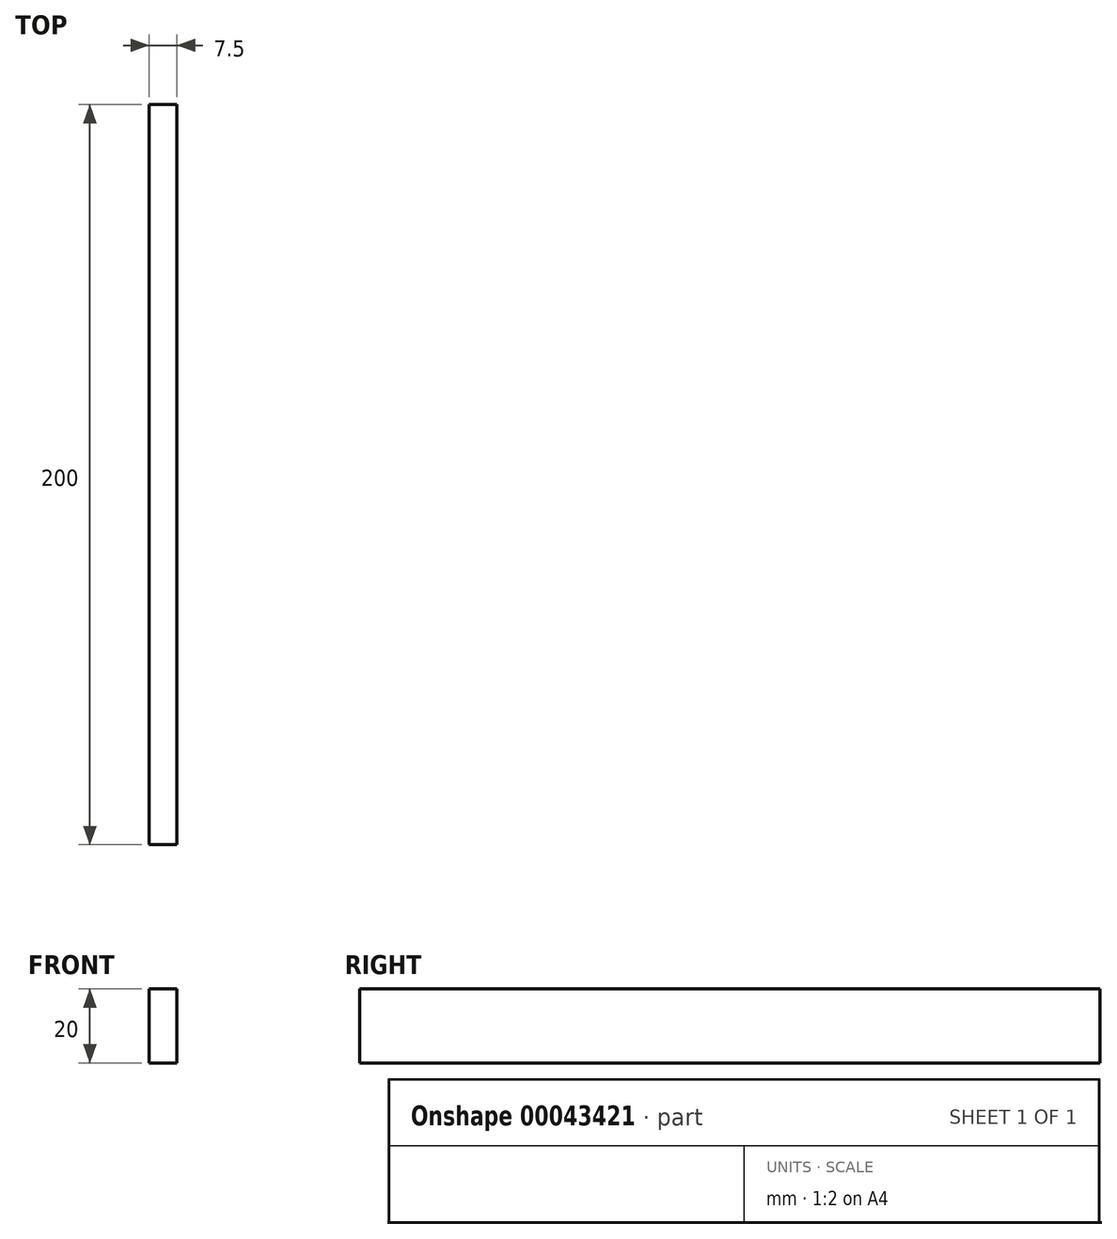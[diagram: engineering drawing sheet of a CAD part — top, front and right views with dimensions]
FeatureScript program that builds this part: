
annotation { "Feature Type Name" : "Feature", "Feature Type Description" : "" }
export const myFeature = defineFeature(function(context is Context, id is Id, definition is map)
    precondition{}
    {
        {
            var Q0;
            Q0=qCreatedBy(makeId("Front.planeOp"),FACE);
            var sketch = newSketch(context, id + "F0", { "sketchPlane" : qUnion([Q0])});
            skLineSegment(sketch, "E0.rect.bottom", {"start": v(3.75, 10) * mm, "end": v(-3.75, 10) * mm});
            skLineSegment(sketch, "E0.rect.top", {"start": v(3.75, -10) * mm, "end": v(-3.75, -10) * mm});
            skLineSegment(sketch, "E0.rect.left", {"start": v(3.75, 10) * mm, "end": v(3.75, -10) * mm});
            skLineSegment(sketch, "E0.rect.right", {"start": v(-3.75, 10) * mm, "end": v(-3.75, -10) * mm});
            skPoint(sketch, "E0.rect.middle", {"position": v(0, 0) * mm});
            skSolve(sketch);
        }
        {
            var Q0;
            Q0=qSketchRegion(id+"F0",true);
            extrude(context, id + "F1", {"entities" : qUnion([Q0]), "depth" : 200 * mm});
        }
    });
